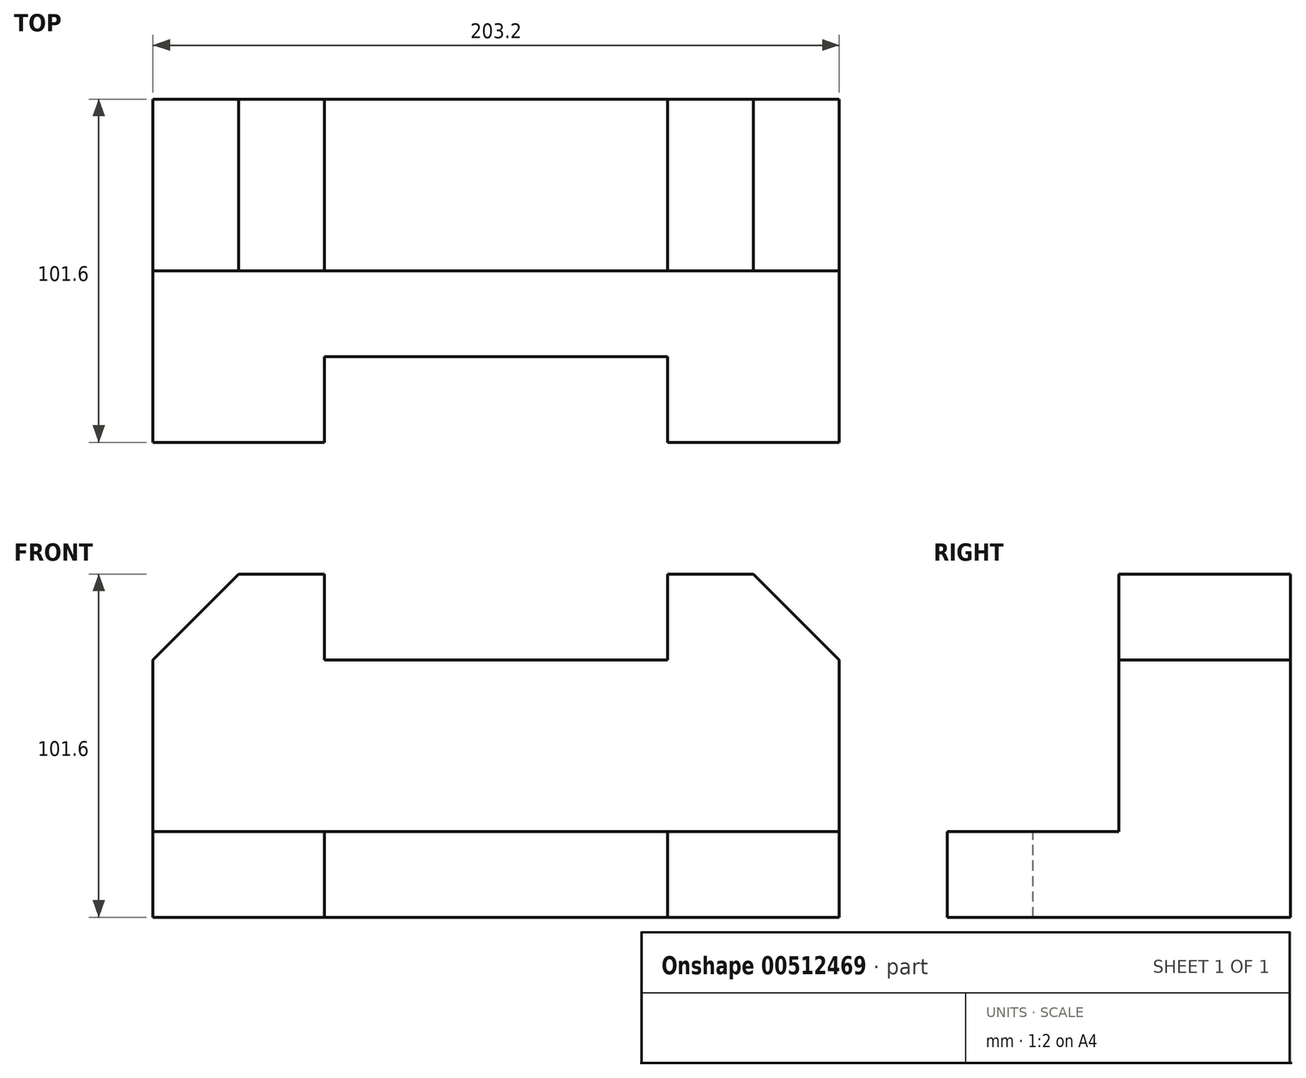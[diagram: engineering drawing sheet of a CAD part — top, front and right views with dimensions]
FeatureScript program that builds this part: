
annotation { "Feature Type Name" : "Feature", "Feature Type Description" : "" }
export const myFeature = defineFeature(function(context is Context, id is Id, definition is map)
    precondition{}
    {
        {
            var Q0;
            Q0=qCreatedBy(makeId("Front.planeOp"),FACE);
            var sketch = newSketch(context, id + "F0", { "sketchPlane" : qUnion([Q0])});
            skLineSegment(sketch, "E0.bottom", {"start": v(0, 0) * mm, "end": v(203.2, 0) * mm});
            skLineSegment(sketch, "E0.top", {"start": v(0, 76.2) * mm, "end": v(203.2, 76.2) * mm});
            skLineSegment(sketch, "E0.left", {"start": v(0, 0) * mm, "end": v(0, 76.2) * mm});
            skLineSegment(sketch, "E0.right", {"start": v(203.2, 0) * mm, "end": v(203.2, 76.2) * mm});
            skSolve(sketch);
        }
        {
            var Q0;
            Q0=makeQuery(id+"F0.imprint","IMPRINT",FACE,{"disambiguationData":[TD([[makeQuery(id+"F0.imprint","IMPRINT",EDGE,{"derivedFrom":sQuery(id+"F0.wireOp",EDGE,"E0.bottom")}),1.0]])]});
            extrude(context, id + "F1", {"entities" : qUnion([Q0]), "depth" : 50.8 * mm});
        }
        {
            var Q0;
            Q0=makeQuery(id+"F1.opExtrude","CAP_FACE",FACE,{"disambiguationData":[OSD([sQuery(id+"F0.wireOp",EDGE,"E0.bottom"),sQuery(id+"F0.wireOp",EDGE,"E0.top"),sQuery(id+"F0.wireOp",EDGE,"E0.left"),sQuery(id+"F0.wireOp",EDGE,"E0.right")])],"isStart":false});
            var sketch = newSketch(context, id + "F2", { "sketchPlane" : qUnion([Q0])});
            skLineSegment(sketch, "E1.bottom", {"start": v(0, 0) * mm, "end": v(203.2, 0) * mm});
            skLineSegment(sketch, "E1.top", {"start": v(0, 25.4) * mm, "end": v(203.2, 25.4) * mm});
            skLineSegment(sketch, "E1.left", {"start": v(0, 0) * mm, "end": v(0, 25.4) * mm});
            skLineSegment(sketch, "E1.right", {"start": v(203.2, 0) * mm, "end": v(203.2, 25.4) * mm});
            skSolve(sketch);
        }
        {
            var Q0;
            Q0=makeQuery(id+"F2.imprint","IMPRINT",FACE,{"disambiguationData":[TD([[makeQuery(id+"F2.imprint","IMPRINT",EDGE,{"derivedFrom":sQuery(id+"F2.wireOp",EDGE,"E1.bottom")}),1.0]])]});
            extrude(context, id + "F3", {"entities" : qUnion([Q0]), "operationType" : NewBodyOperationType.ADD, "depth" : 25.4 * mm});
        }
        {
            var Q0;
            Q0=makeQuery(id+"F3.opExtrude","CAP_FACE",FACE,{"disambiguationData":[OSD([sQuery(id+"F2.wireOp",EDGE,"E1.bottom"),sQuery(id+"F2.wireOp",EDGE,"E1.top"),sQuery(id+"F2.wireOp",EDGE,"E1.left"),sQuery(id+"F2.wireOp",EDGE,"E1.right")])],"isStart":false});
            var sketch = newSketch(context, id + "F4", { "sketchPlane" : qUnion([Q0])});
            skLineSegment(sketch, "E2.bottom", {"start": v(0, 0) * mm, "end": v(50.8, 0) * mm});
            skLineSegment(sketch, "E2.top", {"start": v(0, 25.4) * mm, "end": v(50.8, 25.4) * mm});
            skLineSegment(sketch, "E2.left", {"start": v(0, 0) * mm, "end": v(0, 25.4) * mm});
            skLineSegment(sketch, "E2.right", {"start": v(50.8, 0) * mm, "end": v(50.8, 25.4) * mm});
            skSolve(sketch);
        }
        {
            var Q0;
            Q0=makeQuery(id+"F4.imprint","IMPRINT",FACE,{"disambiguationData":[TD([[makeQuery(id+"F4.imprint","IMPRINT",EDGE,{"derivedFrom":sQuery(id+"F4.wireOp",EDGE,"E2.bottom")}),1.0]])]});
            extrude(context, id + "F5", {"entities" : qUnion([Q0]), "operationType" : NewBodyOperationType.ADD, "depth" : 25.4 * mm});
        }
        {
            var Q0;
            Q0=makeQuery(id+"F3.opExtrude","CAP_FACE",FACE,{"disambiguationData":[OSD([sQuery(id+"F2.wireOp",EDGE,"E1.bottom"),sQuery(id+"F2.wireOp",EDGE,"E1.top"),sQuery(id+"F2.wireOp",EDGE,"E1.left"),sQuery(id+"F2.wireOp",EDGE,"E1.right")])],"isStart":false});
            var sketch = newSketch(context, id + "F6", { "sketchPlane" : qUnion([Q0])});
            skLineSegment(sketch, "E3.bottom", {"start": v(203.2, 0) * mm, "end": v(152.4, 0) * mm});
            skLineSegment(sketch, "E3.top", {"start": v(203.2, 25.4) * mm, "end": v(152.4, 25.4) * mm});
            skLineSegment(sketch, "E3.left", {"start": v(203.2, 0) * mm, "end": v(203.2, 25.4) * mm});
            skLineSegment(sketch, "E3.right", {"start": v(152.4, 0) * mm, "end": v(152.4, 25.4) * mm});
            skSolve(sketch);
        }
        {
            var Q0;
            Q0=makeQuery(id+"F6.imprint","IMPRINT",FACE,{"disambiguationData":[TD([[makeQuery(id+"F6.imprint","IMPRINT",EDGE,{"derivedFrom":sQuery(id+"F6.wireOp",EDGE,"E3.bottom")}),1.0]])]});
            extrude(context, id + "F7", {"entities" : qUnion([Q0]), "operationType" : NewBodyOperationType.ADD, "depth" : 25.4 * mm});
        }
        {
            var Q0;
            Q0=makeQuery(id+"F1.opExtrude","SWEPT_FACE",FACE,{"disambiguationData":[OSD([sQuery(id+"F0.wireOp",EDGE,"E0.top")])]});
            var sketch = newSketch(context, id + "F8", { "sketchPlane" : qUnion([Q0])});
            skLineSegment(sketch, "E4.bottom", {"start": v(0, 0) * mm, "end": v(25.4, 0) * mm});
            skLineSegment(sketch, "E4.top", {"start": v(0, -50.8) * mm, "end": v(25.4, -50.8) * mm});
            skLineSegment(sketch, "E4.left", {"start": v(0, 0) * mm, "end": v(0, -50.8) * mm});
            skLineSegment(sketch, "E4.right", {"start": v(25.4, 0) * mm, "end": v(25.4, -50.8) * mm});
            skSolve(sketch);
        }
        {
            var Q0;
            Q0 = qSketchRegion(id + "F8", true);
            extrude(context, id + "F9", {"entities" : qUnion([Q0]), "operationType" : NewBodyOperationType.ADD, "depth" : 25.4 * mm});
        }
        {
            var Q0;
            Q0=makeQuery(id+"F9.opExtrude","CAP_EDGE",EDGE,{"disambiguationData":[OSD([sQuery(id+"F8.wireOp",EDGE,"E4.left")])],"isStart":false});
            chamfer(context, id + "F10", {"entities" : qUnion([Q0]), "width" : 25.4 * mm, "tangentPropagation" : true});
        }
        {
            var Q0;
            Q0=makeQuery(id+"F1.opExtrude","SWEPT_FACE",FACE,{"disambiguationData":[OSD([sQuery(id+"F0.wireOp",EDGE,"E0.top")])]});
            var sketch = newSketch(context, id + "F11", { "sketchPlane" : qUnion([Q0])});
            skLineSegment(sketch, "E5.bottom", {"start": v(25.4, 0) * mm, "end": v(50.8, 0) * mm});
            skLineSegment(sketch, "E5.top", {"start": v(25.4, -50.8) * mm, "end": v(50.8, -50.8) * mm});
            skLineSegment(sketch, "E5.left", {"start": v(25.4, 0) * mm, "end": v(25.4, -50.8) * mm});
            skLineSegment(sketch, "E5.right", {"start": v(50.8, 0) * mm, "end": v(50.8, -50.8) * mm});
            skSolve(sketch);
        }
        {
            var Q0;
            Q0=makeQuery(id+"F11.imprint","IMPRINT",FACE,{"disambiguationData":[TD([[makeQuery(id+"F11.imprint","IMPRINT",EDGE,{"derivedFrom":sQuery(id+"F11.wireOp",EDGE,"E5.bottom")}),-1.0]])]});
            extrude(context, id + "F12", {"entities" : qUnion([Q0]), "operationType" : NewBodyOperationType.ADD, "depth" : 25.4 * mm});
        }
        {
            var Q0;
            Q0=makeQuery(id+"F1.opExtrude","SWEPT_FACE",FACE,{"disambiguationData":[OSD([sQuery(id+"F0.wireOp",EDGE,"E0.top")])]});
            var sketch = newSketch(context, id + "F13", { "sketchPlane" : qUnion([Q0])});
            skLineSegment(sketch, "E6.bottom", {"start": v(203.2, 0) * mm, "end": v(177.8, 0) * mm});
            skLineSegment(sketch, "E6.top", {"start": v(203.2, -50.8) * mm, "end": v(177.8, -50.8) * mm});
            skLineSegment(sketch, "E6.left", {"start": v(203.2, 0) * mm, "end": v(203.2, -50.8) * mm});
            skLineSegment(sketch, "E6.right", {"start": v(177.8, 0) * mm, "end": v(177.8, -50.8) * mm});
            skSolve(sketch);
        }
        {
            var Q0;
            Q0=makeQuery(id+"F13.imprint","IMPRINT",FACE,{"disambiguationData":[TD([[makeQuery(id+"F13.imprint","IMPRINT",EDGE,{"derivedFrom":sQuery(id+"F13.wireOp",EDGE,"E6.bottom")}),-1.0]])]});
            extrude(context, id + "F14", {"entities" : qUnion([Q0]), "operationType" : NewBodyOperationType.ADD, "depth" : 25.4 * mm});
        }
        {
            var Q0;
            Q0=makeQuery(id+"F14.opExtrude","CAP_EDGE",EDGE,{"disambiguationData":[OSD([sQuery(id+"F13.wireOp",EDGE,"E6.left")])],"isStart":false});
            chamfer(context, id + "F15", {"entities" : qUnion([Q0]), "width" : 25.4 * mm, "tangentPropagation" : true});
        }
        {
            var Q0;
            Q0=makeQuery(id+"F1.opExtrude","SWEPT_FACE",FACE,{"disambiguationData":[OSD([sQuery(id+"F0.wireOp",EDGE,"E0.top")])]});
            var sketch = newSketch(context, id + "F16", { "sketchPlane" : qUnion([Q0])});
            skLineSegment(sketch, "E7.bottom", {"start": v(177.8, 0) * mm, "end": v(152.4, 0) * mm});
            skLineSegment(sketch, "E7.top", {"start": v(177.8, -50.8) * mm, "end": v(152.4, -50.8) * mm});
            skLineSegment(sketch, "E7.left", {"start": v(177.8, 0) * mm, "end": v(177.8, -50.8) * mm});
            skLineSegment(sketch, "E7.right", {"start": v(152.4, 0) * mm, "end": v(152.4, -50.8) * mm});
            skSolve(sketch);
        }
        {
            var Q0;
            Q0=makeQuery(id+"F16.imprint","IMPRINT",FACE,{"disambiguationData":[TD([[makeQuery(id+"F16.imprint","IMPRINT",EDGE,{"derivedFrom":sQuery(id+"F16.wireOp",EDGE,"E7.bottom")}),-1.0]])]});
            extrude(context, id + "F17", {"entities" : qUnion([Q0]), "operationType" : NewBodyOperationType.ADD, "depth" : 25.4 * mm});
        }
    });
